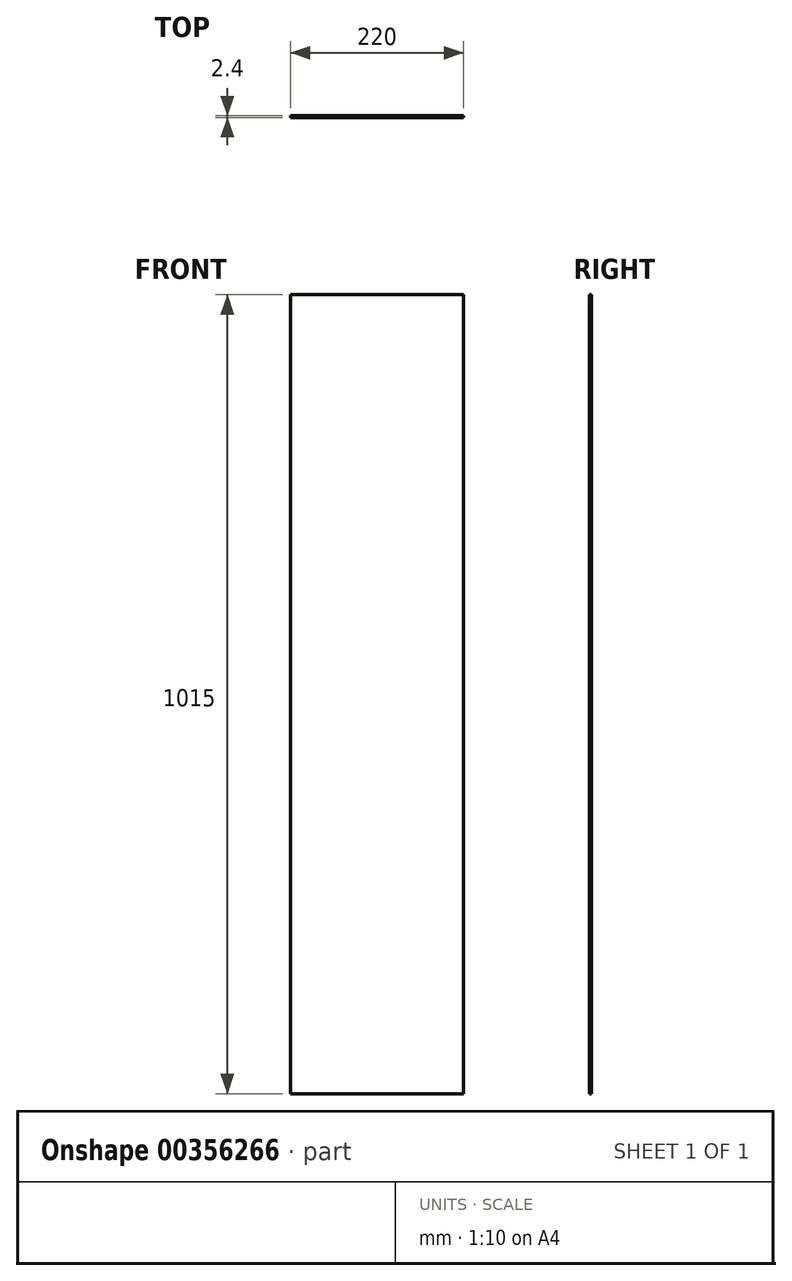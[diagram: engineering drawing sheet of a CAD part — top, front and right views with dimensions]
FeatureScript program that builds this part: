
annotation { "Feature Type Name" : "Feature", "Feature Type Description" : "" }
export const myFeature = defineFeature(function(context is Context, id is Id, definition is map)
    precondition{}
    {
        {
            var Q0;
            Q0=qCreatedBy(makeId("Front.planeOp"),FACE);
            var sketch = newSketch(context, id + "F0", { "sketchPlane" : qUnion([Q0])});
            skLineSegment(sketch, "E0.bottom", {"start": v(-30.03, 969.38) * mm, "end": v(189.97, 969.38) * mm});
            skLineSegment(sketch, "E0.top", {"start": v(-30.03, -45.62) * mm, "end": v(189.97, -45.62) * mm});
            skLineSegment(sketch, "E0.left", {"start": v(-30.03, 969.38) * mm, "end": v(-30.03, -45.62) * mm});
            skLineSegment(sketch, "E0.right", {"start": v(189.97, 969.38) * mm, "end": v(189.97, -45.62) * mm});
            skSolve(sketch);
        }
        {
            var Q0;
            Q0 = qSketchRegion(id + "F0", true);
            extrude(context, id + "F1", {"entities" : qUnion([Q0]), "depth" : 2.4 * mm});
        }
    });
